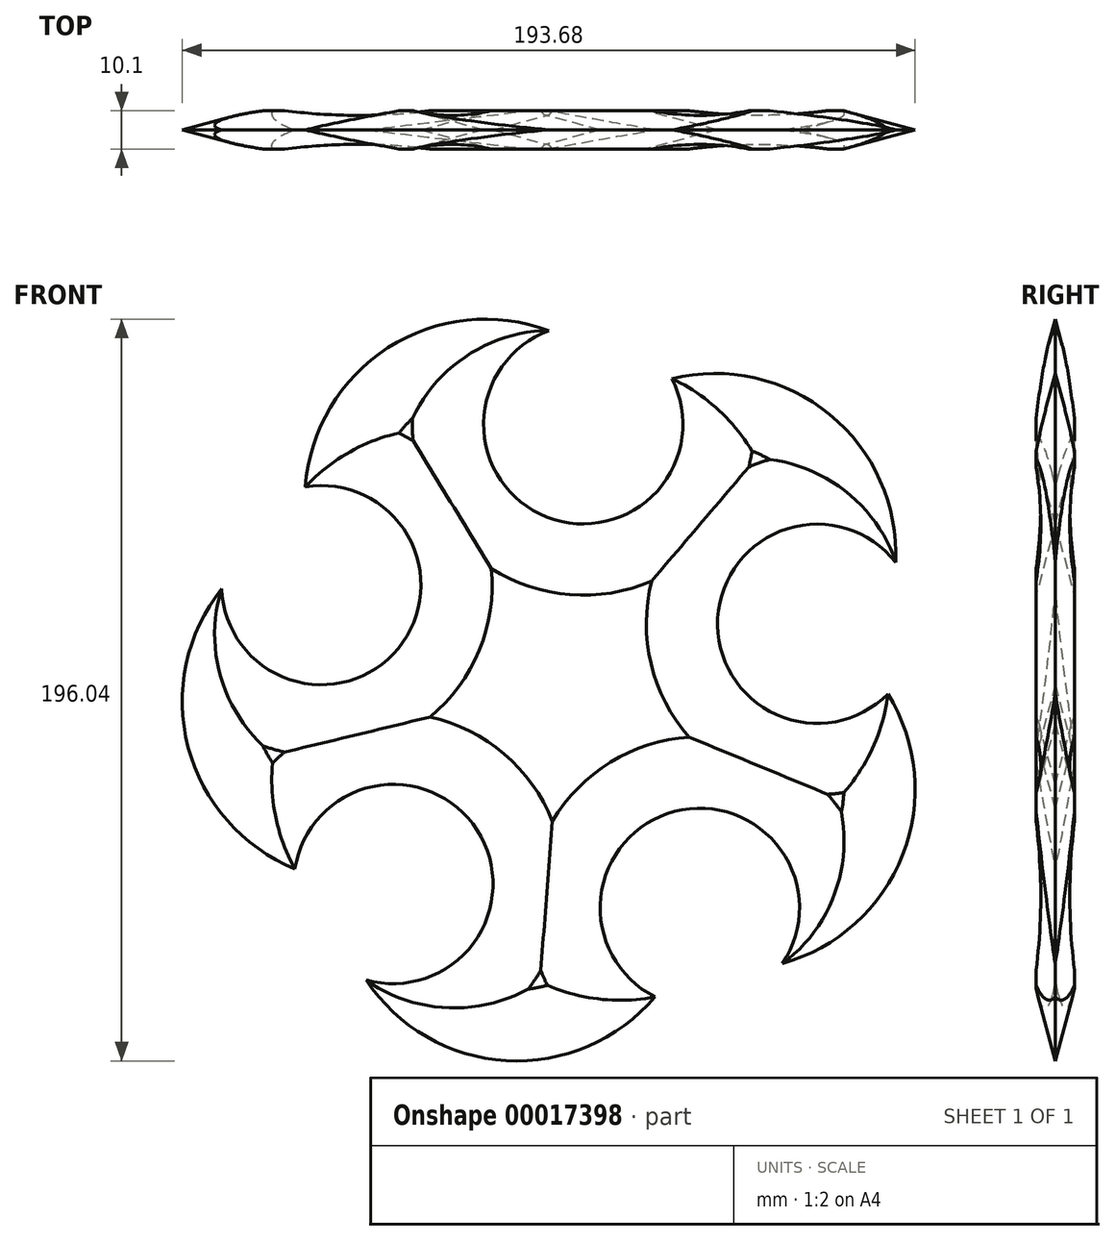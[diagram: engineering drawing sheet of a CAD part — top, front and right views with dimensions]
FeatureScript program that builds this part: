
annotation { "Feature Type Name" : "Feature", "Feature Type Description" : "" }
export const myFeature = defineFeature(function(context is Context, id is Id, definition is map)
    precondition{}
    {
        {
            var Q0;
            Q0=qCreatedBy(makeId("Front.planeOp"),FACE);
            var sketch = newSketch(context, id + "F0", { "sketchPlane" : qUnion([Q0])});
            skLineSegment(sketch, "E0", {"start": v(0, 93.35) * mm, "end": v(5.36, 68.9) * mm});
            skLineSegment(sketch, "E1.1.0", {"start": v(-88.78, 28.85) * mm, "end": v(-63.88, 26.39) * mm});
            skLineSegment(sketch, "E1.2.0", {"start": v(-54.87, -75.52) * mm, "end": v(-44.84, -52.6) * mm});
            skLineSegment(sketch, "E1.3.0", {"start": v(54.87, -75.52) * mm, "end": v(36.17, -58.9) * mm});
            skLineSegment(sketch, "E1.4.0", {"start": v(88.78, 28.85) * mm, "end": v(67.2, 16.2) * mm});
            skPoint(sketch, "E1.center", {"position": v(0, 0) * mm});
            skArc(sketch, "E2.trimOffspring", {"start": v(67.2, 16.2) * mm, "mid": v(93.79, -34.06) * mm, "end": v(54.87, -75.52) * mm});
            skArc(sketch, "E3.trimOffspring", {"start": v(36.17, -58.9) * mm, "mid": v(-3.41, -99.72) * mm, "end": v(-54.87, -75.52) * mm});
            skArc(sketch, "E4.trimOffspring", {"start": v(5.36, 68.9) * mm, "mid": v(61.38, 78.67) * mm, "end": v(88.78, 28.85) * mm});
            skArc(sketch, "E5.trimOffspring", {"start": v(-44.84, -52.6) * mm, "mid": v(-95.9, -27.57) * mm, "end": v(-88.78, 28.85) * mm});
            skArc(sketch, "E6.trimOffspring", {"start": v(-63.88, 26.39) * mm, "mid": v(-55.85, 82.68) * mm, "end": v(0, 93.35) * mm});
            skSolve(sketch);
        }
        {
            var Q0;
            Q0=makeQuery(id+"F0.imprint","IMPRINT",FACE,{"disambiguationData":[TD([[makeQuery(id+"F0.imprint","IMPRINT",EDGE,{"derivedFrom":sQuery(id+"F0.wireOp",EDGE,"E0")}),-1.0]])]});
            extrude(context, id + "F1", {"entities" : qUnion([Q0]), "depth" : 10.1 * mm});
        }
        {
            var Q0;
            Q0=makeQuery(id+"F1.opExtrude","CAP_FACE",FACE,{"disambiguationData":[OSD([sQuery(id+"F0.wireOp",EDGE,"E0"),sQuery(id+"F0.wireOp",EDGE,"E1.1.0"),sQuery(id+"F0.wireOp",EDGE,"E1.2.0"),sQuery(id+"F0.wireOp",EDGE,"E1.3.0"),sQuery(id+"F0.wireOp",EDGE,"E1.4.0"),sQuery(id+"F0.wireOp",EDGE,"E2.trimOffspring"),sQuery(id+"F0.wireOp",EDGE,"E3.trimOffspring"),sQuery(id+"F0.wireOp",EDGE,"E4.trimOffspring"),sQuery(id+"F0.wireOp",EDGE,"E5.trimOffspring"),sQuery(id+"F0.wireOp",EDGE,"E6.trimOffspring")])],"isStart":false});
            var sketch = newSketch(context, id + "F2", { "sketchPlane" : qUnion([Q0])});
            skCircle(sketch, "E7", {"center": v(5.36, 68.9) * mm, "radius": 25.18 * mm});
            skCircle(sketch, "E8.1.0", {"center": v(-63.88, 26.39) * mm, "radius": 25.18 * mm});
            skCircle(sketch, "E8.2.0", {"center": v(-44.84, -52.6) * mm, "radius": 25.18 * mm});
            skCircle(sketch, "E8.3.0", {"center": v(36.17, -58.9) * mm, "radius": 25.18 * mm});
            skCircle(sketch, "E8.4.0", {"center": v(67.2, 16.2) * mm, "radius": 25.18 * mm});
            skPoint(sketch, "E8.center", {"position": v(0, 0) * mm});
            skSolve(sketch);
        }
        {
            var Q0;
            {var subQ3=makeQuery(id+"F1.opExtrude","CAP_EDGE",EDGE,{"disambiguationData":[OSD([sQuery(id+"F0.wireOp",EDGE,"E0")])],"isStart":false});Q0=makeQuery(id+"F2.imprint","IMPRINT",FACE,{"disambiguationData":[TD([[makeQuery(id+"F2.imprint","IMPRINT",EDGE,{"derivedFrom":subQ3}),-1.0]])]});}
            var Q1;
            {var subQ3=makeQuery(id+"F1.opExtrude","CAP_EDGE",EDGE,{"disambiguationData":[OSD([sQuery(id+"F0.wireOp",EDGE,"E1.4.0")])],"isStart":false});Q1=makeQuery(id+"F2.imprint","IMPRINT",FACE,{"disambiguationData":[TD([[makeQuery(id+"F2.imprint","IMPRINT",EDGE,{"derivedFrom":subQ3}),-1.0]])]});}
            var Q2;
            {var subQ3=makeQuery(id+"F1.opExtrude","CAP_EDGE",EDGE,{"disambiguationData":[OSD([sQuery(id+"F0.wireOp",EDGE,"E1.3.0")])],"isStart":false});Q2=makeQuery(id+"F2.imprint","IMPRINT",FACE,{"disambiguationData":[TD([[makeQuery(id+"F2.imprint","IMPRINT",EDGE,{"derivedFrom":subQ3}),-1.0]])]});}
            var Q3;
            {var subQ3=makeQuery(id+"F1.opExtrude","CAP_EDGE",EDGE,{"disambiguationData":[OSD([sQuery(id+"F0.wireOp",EDGE,"E1.2.0")])],"isStart":false});Q3=makeQuery(id+"F2.imprint","IMPRINT",FACE,{"disambiguationData":[TD([[makeQuery(id+"F2.imprint","IMPRINT",EDGE,{"derivedFrom":subQ3}),-1.0]])]});}
            var Q4;
            {var subQ3=makeQuery(id+"F1.opExtrude","CAP_EDGE",EDGE,{"disambiguationData":[OSD([sQuery(id+"F0.wireOp",EDGE,"E1.1.0")])],"isStart":false});Q4=makeQuery(id+"F2.imprint","IMPRINT",FACE,{"disambiguationData":[TD([[makeQuery(id+"F2.imprint","IMPRINT",EDGE,{"derivedFrom":subQ3}),-1.0]])]});}
            extrude(context, id + "F3", {"entities" : qUnion([Q0, Q1, Q2, Q3, Q4]), "operationType" : NewBodyOperationType.REMOVE, "endBound" : BoundingType.THROUGH_ALL, "oppositeDirection" : true, "depth" : 25 * mm});
        }
        {
            var Q0;
            Q0=makeQuery(id+"F1.opExtrude","CAP_FACE",FACE,{"disambiguationData":[OSD([sQuery(id+"F0.wireOp",EDGE,"E0"),sQuery(id+"F0.wireOp",EDGE,"E1.1.0"),sQuery(id+"F0.wireOp",EDGE,"E1.2.0"),sQuery(id+"F0.wireOp",EDGE,"E1.3.0"),sQuery(id+"F0.wireOp",EDGE,"E1.4.0"),sQuery(id+"F0.wireOp",EDGE,"E2.trimOffspring"),sQuery(id+"F0.wireOp",EDGE,"E3.trimOffspring"),sQuery(id+"F0.wireOp",EDGE,"E4.trimOffspring"),sQuery(id+"F0.wireOp",EDGE,"E5.trimOffspring"),sQuery(id+"F0.wireOp",EDGE,"E6.trimOffspring")])],"isStart":false});
            chamfer(context, id + "F4", {"entities" : qUnion([Q0]), "chamferType" : ChamferType.OFFSET_ANGLE, "width" : 20 * mm, "oppositeDirection" : true, "angle" : 15 * degree, "tangentPropagation" : true});
        }
        {
            var Q0;
            Q0=makeQuery(id+"F1.opExtrude","CAP_FACE",FACE,{"disambiguationData":[OSD([sQuery(id+"F0.wireOp",EDGE,"E0"),sQuery(id+"F0.wireOp",EDGE,"E1.1.0"),sQuery(id+"F0.wireOp",EDGE,"E1.2.0"),sQuery(id+"F0.wireOp",EDGE,"E1.3.0"),sQuery(id+"F0.wireOp",EDGE,"E1.4.0"),sQuery(id+"F0.wireOp",EDGE,"E2.trimOffspring"),sQuery(id+"F0.wireOp",EDGE,"E3.trimOffspring"),sQuery(id+"F0.wireOp",EDGE,"E4.trimOffspring"),sQuery(id+"F0.wireOp",EDGE,"E5.trimOffspring"),sQuery(id+"F0.wireOp",EDGE,"E6.trimOffspring")])],"isStart":true});
            chamfer(context, id + "F5", {"entities" : qUnion([Q0]), "chamferType" : ChamferType.OFFSET_ANGLE, "width" : 20 * mm, "oppositeDirection" : false, "angle" : 15 * degree, "tangentPropagation" : true});
        }
    });
